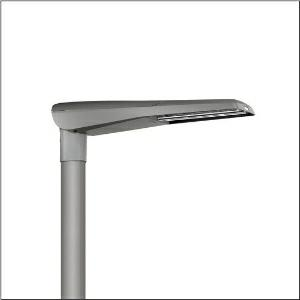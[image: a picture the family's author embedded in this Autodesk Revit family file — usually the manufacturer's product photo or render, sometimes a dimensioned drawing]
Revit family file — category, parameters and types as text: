
# Revit family: streetlight_sl_11_iq_mini___st1_2p1_0_5xc2gc1f08he_badf
name_source: partatom
category: Lighting Fixtures
units: mm (PartAtom-declared; Revit-internal decimal feet)

## family parameters
Cut with Voids When Loaded = No
Host = Face
Light Source = No
Part Type = Normal
Room Calculation Point = No
Round Connector Dimension = Use Diameter
Shared = No

## types (1)
- --- (1 x LED, 6750 lm, 63 W, 2200K)
    Apparent Load = 63 VA
    CIE Flux Codes = 31 68 95 100 100
    Color Rendering = 70
    Color Temperature = 2200K
    Default Elevation = 1800 mm
    Description = Streetlight SL 11 iQ mini, mast luminaire, primary light control with 3 zone facetted reflector, of plastic, silver coated, highly specular, primary optical cover: cover, of PMMA, transparent, light distribution: ST1.2P1.0, light emission: direct distribution, primary light characteristic: asymmetric, installation type: post-top, side-entry, lamps: LED, High Power LED, rated values: 8.240lm | 61,5W | 134lm/W (begin service life); end service life: 8.240lm | 64,5W; at 50% lumin. flux: 4.120lm | 29,1W | 141,6lm/W, colour temperature: 2200/2700/3000/4000K, colour rendering: CRI > 70, light colour: 722/727/730/740, light setting 1 begin service life: 100% | 8.240lm | 61,5W | 134lm/W | 3.000K, light setting 1 end service life: 64,5W, further light settings possible, control: Street-Remote, Auto-Match, Temp-Guard, Lumen-Switch, Night-Set, Smart-Wire, Light-Fading, Desk-Remote (wireless, voltage-free reading and setting of iQ features in the workshop via application-optimized NFC function/RFID function), optimised constant luminous flux control (CLO 2.0), with cable H07RN-F 5x 1.5mm², mains connection: 230..240V, AC, 50/60Hz, connection cable pre-assembled, cable length: 8,5m, luminaire housing, of diecast aluminium, powder-coated, Siteco® metallic grey (DB 702S), please order mast flange separately, inclination adjustable without tools: 0°, 5°, 10°, 15° (post-top) | 0°, -5°, -10°, -15° (side-entry), sealing non-destructively replaceable, multi-level sealing system, length: 736mm, width: 174mm, height: 116mm, mast flange for spigot size: 42mm (side-entry): 5XC10008XM4, 60/48mm (side-entry/post-top): 5XC10108XM2, 76/60mm (side-entry/post-top): 5XC10108XM1, equipment: Power, protection rating (complete): IP66, insulation class (complete): insulation class II (safety insulation), certification: CE, ENEC, ENEC+, VDE, impact resistance: IK10, permissible operating ambient temperature for outdoor applications: -25..+50°C, standard-compliant lighting for roads and squares, Environmental Product Declaration (EPD) tested and certified by an independent institute, packaging unit: 1 piece

Light Distribution: ST1.2P1.0
    Height = 116 mm
    Lamp = 1 x LED
    Lamp Light Flux = 6750 lm
    Lamp Power = 63 W
    Lamp count = 1
    Length = 736 mm
    Luminous efficacy = 107 lm/W
    Manufacturer = Siteco
    ModVariant = No
    Model = 5XC2GC1F08HE
    Number of Poles = 1
    OnlyDefault = Yes
    Power Factor = 1
    Product Name = Streetlight SL 11 iQ mini | ST1.2P1.0
    Product group = mast luminaire | pylon top
    ProductGroupID = 6100
    Protection Class = Protection class II
    Protection Degree = IP 66
    RLX_Detail_Level = 1
    RLX_Emergency_Light_Flux = 0 lm
    RLX_Emergency_Type = 0
    RLX_Emergency_Type_DB = No
    RlxData = <blob elided: 53769 chars, md5=48ad17a7>
    Socket = socket
    Standby Power = 0 W
    System Light Flux = 6750 lm
    System Power = 63 W
    Type Comments = individual setting: luminous flux: 100 % | dim-lin: 254 | 858 mA
    Type Image = l_1003508.jpg
    URL = http://relux.com
    VarID = @adj_054799
    Voltage = 0 V
    Weight = 0.00 kg
    Width = 174 mm

## geometry (parser evidence)
native form markers: Blend x4, Sweep x11
no freeform markers — native parametric forms only
